# Revit family: VAD_Roof_Exhauster
name_source: partatom
category: Mechanical Equipment
units: mm (PartAtom-declared; Revit-internal decimal feet)

## family parameters
Always vertical = Yes
Cut with Voids When Loaded = No
Part Type = Normal
Room Calculation Point = No
Round Connector Dimension = Use Diameter
Shared = No
Work Plane-Based = No

## types (9) — shared parameters
0 = 0' - 0"
1" = 0' - 1"
1.5 = 0' - 1 1/2"
2" = 0' - 2"
2' = 2' - 0"
3" = 0' - 3"
30 = 30.00°
4" = 0' - 4"
60 = 60.00°
Manufacturer = Loren Cook Company
Model = VAD
ONE EIGTH = 0' - 0 1/8"
P = 0' - 0 9/16"
P/2 = 0' - 0 9/32"
Type Comments = Fixed Pitch Vane Axial Roof Exhauster Direct Drive Arrangement 4
URL = www.lorencook.com

## per-type parameters (varying)
- 18_VAD_ROOF_EXHAUSTER: (A+.25")/2=0' - 9 1/8"; (B/2)+2"=1' - 0 5/8"; (E-.25")/2=0' - 9 3/8"; (E/2)-2"=0' - 7 1/2"; (H-(A/2))/2=0' - 9 1/8"; (T_SQ+.25")/2=1' - 2 1/8"; -(E-.25")/2=-0' - 9 3/8"; -(E/2)+2"=-0' - 7 1/2"; -E/2=-0' - 9 1/2"; A=1' - 6"; A/2=0' - 9"; A/3=0' - 7 3/16"; B=1' - 9 1/4"; B/2=0' - 10 5/8"; C=1' - 7 3/4"; C/2=0' - 9 7/8"; C/2+L=1' - 10 5/16"; E=1' - 7"; E-2"=1' - 5"; E/2=0' - 9 1/2"; F=0' - 0 7/16"; F/2=0' - 0 7/32"; G=12' - 0"; H=2' - 3 1/4"; H+L=3' - 3 11/16"; H-(A/2)=1' - 6 1/4"; J=0' - 0 7/8"; J+J=0' - 1 3/4"; K=2' - 3 1/4"; K/2=1' - 1 5/8"; L=1' - 0 7/16"; L-(C/2)=0' - 2 9/16"; L-.125"=1' - 0 5/16"; M=1' - 9"; M/2=0' - 10 1/2"; N=0' - 8 1/2"; RO=1' - 11 1/2"; RO/2=0' - 11 3/4"; T_SQ=2' - 4"; UP_A=3' - 5"
- 21_VAD_ROOF_EXHAUSTER: (A+.25")/2=0' - 10 5/8"; (B/2)+2"=1' - 2 1/8"; (E-.25")/2=0' - 9 7/8"; (E/2)-2"=0' - 8"; (H-(A/2))/2=0' - 10 1/2"; (T_SQ+.25")/2=1' - 4 1/8"; -(E-.25")/2=-0' - 9 7/8"; -(E/2)+2"=-0' - 8"; -E/2=-0' - 10"; A=1' - 9"; A/2=0' - 10 1/2"; A/3=0' - 8 13/32"; B=2' - 0 1/4"; B/2=1' - 0 1/8"; C=1' - 10 3/4"; C/2=0' - 11 3/8"; C/2+L=2' - 1 5/16"; E=1' - 8"; E-2"=1' - 6"; E/2=0' - 10"; F=0' - 0 7/16"; F/2=0' - 0 7/32"; G=12' - 0"; H=2' - 7 1/2"; H+L=3' - 9 7/16"; H-(A/2)=1' - 9"; J=0' - 0 7/8"; J+J=0' - 1 3/4"; K=2' - 5 1/4"; K/2=1' - 2 5/8"; L=1' - 1 15/16"; L-(C/2)=0' - 2 9/16"; L-.125"=1' - 1 13/16"; M=2' - 0"; M/2=1' - 0"; N=0' - 10"; RO=2' - 3 1/2"; RO/2=1' - 1 3/4"; T_SQ=2' - 8"; UP_A=3' - 6"
- 26_VAD_ROOF_EXHAUSTER: (A+.25")/2=1' - 1 1/8"; (B/2)+2"=1' - 5 5/32"; (E-.25")/2=0' - 10 7/8"; (E/2)-2"=0' - 9"; (H-(A/2))/2=0' - 10 3/4"; (T_SQ+.25")/2=1' - 6 1/8"; -(E-.25")/2=-0' - 10 7/8"; -(E/2)+2"=-0' - 9"; -E/2=-0' - 11"; A=2' - 2"; A/2=1' - 1"; A/3=0' - 10 13/32"; B=2' - 6 5/16"; B/2=1' - 3 5/32"; C=2' - 4"; C/2=1' - 2"; C/2+L=2' - 6 11/16"; E=1' - 10"; E-2"=1' - 8"; E/2=0' - 11"; F=0' - 0 7/16"; F/2=0' - 0 7/32"; G=12' - 0"; H=2' - 10 1/2"; H+L=4' - 3 3/16"; H-(A/2)=1' - 9 1/2"; J=0' - 0 15/16"; J+J=0' - 1 7/8"; K=2' - 6 1/8"; K/2=1' - 3 1/16"; L=1' - 4 11/16"; L-(C/2)=0' - 2 11/16"; L-.125"=1' - 4 9/16"; M=2' - 5 9/16"; M/2=1' - 2 25/32"; N=1' - 0 13/16"; RO=2' - 7 1/2"; RO/2=1' - 3 3/4"; T_SQ=3' - 0"; UP_A=3' - 9"
- 29_VAD_ROOF_EXHAUSTER: (A+.25")/2=1' - 2 5/8"; (B/2)+2"=1' - 6 21/32"; (E-.25")/2=1' - 0 3/8"; (E/2)-2"=0' - 10 1/2"; (H-(A/2))/2=1' - 1"; (T_SQ+.25")/2=1' - 9 1/8"; -(E-.25")/2=-1' - 0 3/8"; -(E/2)+2"=-0' - 10 1/2"; -E/2=-1' - 0 1/2"; A=2' - 5"; A/2=1' - 2 1/2"; A/3=0' - 11 19/32"; B=2' - 9 5/16"; B/2=1' - 4 21/32"; C=2' - 7"; C/2=1' - 3 1/2"; C/2+L=2' - 9 3/4"; E=2' - 1"; E-2"=1' - 11"; E/2=1' - 0 1/2"; F=0' - 0 7/16"; F/2=0' - 0 7/32"; G=12' - 0"; H=3' - 4 1/2"; H+L=4' - 10 3/4"; H-(A/2)=2' - 2"; J=0' - 0 15/16"; J+J=0' - 1 7/8"; K=2' - 10 1/8"; K/2=1' - 5 1/16"; L=1' - 6 1/4"; L-(C/2)=0' - 2 3/4"; L-.125"=1' - 6 1/8"; M=2' - 8 5/8"; M/2=1' - 4 5/16"; N=1' - 2 5/16"; RO=3' - 1 1/2"; RO/2=1' - 6 3/4"; T_SQ=3' - 6"; UP_A=4' - 0"
- 36_VAD_ROOF_EXHAUSTER: (A+.25")/2=1' - 6 1/8"; (B/2)+2"=1' - 10 5/32"; (E-.25")/2=1' - 3 7/8"; (E/2)-2"=1' - 2"; (H-(A/2))/2=1' - 1 3/4"; (T_SQ+.25")/2=2' - 0 1/8"; -(E-.25")/2=-1' - 3 7/8"; -(E/2)+2"=-1' - 2"; -E/2=-1' - 4"; A=3' - 0"; A/2=1' - 6"; A/3=1' - 2 13/32"; B=3' - 4 5/16"; B/2=1' - 8 5/32"; C=3' - 2"; C/2=1' - 7"; C/2+L=3' - 5 1/4"; E=2' - 8"; E-2"=2' - 6"; E/2=1' - 4"; F=0' - 0 9/16"; F/2=0' - 0 9/32"; G=16' - 0"; H=3' - 9 1/2"; H+L=5' - 7 3/4"; H-(A/2)=2' - 3 1/2"; J=0' - 0 15/16"; J+J=0' - 1 7/8"; K=3' - 4 1/8"; K/2=1' - 8 1/16"; L=1' - 10 1/4"; L-(C/2)=0' - 3 1/4"; L-.125"=1' - 10 1/8"; M=3' - 4 5/8"; M/2=1' - 8 5/16"; N=1' - 6 5/16"; RO=3' - 7 1/2"; RO/2=1' - 9 3/4"; T_SQ=4' - 0"; UP_A=5' - 1"
- 42_VAD_ROOF_EXHAUSTER: (A+.25")/2=1' - 9 1/8"; (B/2)+2"=2' - 0 21/32"; (E-.25")/2=1' - 6 3/8"; (E/2)-2"=1' - 4 1/2"; (H-(A/2))/2=1' - 2 3/4"; (T_SQ+.25")/2=2' - 3 1/8"; -(E-.25")/2=-1' - 6 3/8"; -(E/2)+2"=-1' - 4 1/2"; -E/2=-1' - 6 1/2"; A=3' - 6"; A/2=1' - 9"; A/3=1' - 4 13/16"; B=3' - 9 5/16"; B/2=1' - 10 21/32"; C=3' - 8 3/8"; C/2=1' - 10 3/16"; C/2+L=3' - 11 3/8"; E=3' - 1"; E-2"=2' - 11"; E/2=1' - 6 1/2"; F=0' - 0 9/16"; F/2=0' - 0 9/32"; G=16' - 0"; H=4' - 2 1/2"; H+L=6' - 3 11/16"; H-(A/2)=2' - 5 1/2"; J=0' - 0 15/16"; J+J=0' - 1 7/8"; K=4' - 0 1/8"; K/2=2' - 0 1/16"; L=2' - 1 3/16"; L-(C/2)=0' - 3"; L-.125"=2' - 1 1/16"; M=4' - 0 3/4"; M/2=2' - 0 3/8"; N=1' - 9 3/8"; RO=4' - 1 1/2"; RO/2=2' - 0 3/4"; T_SQ=4' - 6"; UP_A=5' - 6"
- 48_VAD_ROOF_EXHAUSTER: (A+.25")/2=2' - 0 1/8"; (B/2)+2"=2' - 4 19/32"; (E-.25")/2=1' - 8 7/8"; (E/2)-2"=1' - 7"; (H-(A/2))/2=1' - 3"; (T_SQ+.25")/2=2' - 5 1/4"; -(E-.25")/2=-1' - 8 7/8"; -(E/2)+2"=-1' - 7"; -E/2=-1' - 9"; A=4' - 0"; A/2=2' - 0"; A/3=1' - 7 3/16"; B=4' - 5 3/16"; B/2=2' - 2 19/32"; C=4' - 2 1/2"; C/2=2' - 1 1/4"; C/2+L=4' - 5 1/2"; E=3' - 6"; E-2"=3' - 4"; E/2=1' - 9"; F=0' - 0 9/16"; F/2=0' - 0 9/32"; G=16' - 0"; H=4' - 6"; H+L=6' - 10 1/4"; H-(A/2)=2' - 6"; J=0' - 0 15/16"; J+J=0' - 1 7/8"; K=4' - 6 1/8"; K/2=2' - 3 1/16"; L=2' - 4 1/4"; L-(C/2)=0' - 3"; L-.125"=2' - 4 1/8"; M=4' - 4 3/4"; M/2=2' - 2 3/8"; N=2' - 0 3/8"; RO=4' - 5 3/4"; RO/2=2' - 2 7/8"; T_SQ=4' - 10 1/4"; UP_A=6' - 11 1/2"
- 54_VAD_ROOF_EXHAUSTER: (A+.25")/2=2' - 3 1/8"; (B/2)+2"=2' - 7 23/32"; (E-.25")/2=1' - 10 7/8"; (E/2)-2"=1' - 9"; (H-(A/2))/2=1' - 4 1/4"; (T_SQ+.25")/2=2' - 8 1/4"; -(E-.25")/2=-1' - 10 7/8"; -(E/2)+2"=-1' - 9"; -E/2=-1' - 11"; A=4' - 6"; A/2=2' - 3"; A/3=1' - 9 19/32"; B=4' - 11 7/16"; B/2=2' - 5 23/32"; C=4' - 8 1/2"; C/2=2' - 4 1/4"; C/2+L=4' - 11 1/2"; E=3' - 10"; E-2"=3' - 8"; E/2=1' - 11"; F=0' - 0 9/16"; F/2=0' - 0 9/32"; G=16' - 0"; H=4' - 11 1/2"; H+L=7' - 6 3/4"; H-(A/2)=2' - 8 1/2"; J=0' - 1"; J+J=0' - 2"; K=5' - 0"; K/2=2' - 6"; L=2' - 7 1/4"; L-(C/2)=0' - 3"; L-.125"=2' - 7 1/8"; M=4' - 11"; M/2=2' - 5 1/2"; N=2' - 3 1/2"; RO=4' - 11 3/4"; RO/2=2' - 5 7/8"; T_SQ=5' - 4 1/4"; UP_A=7' - 3 1/2"
- 60_VAD_ROOF_EXHAUSTER: (A+.25")/2=2' - 6 1/8"; (B/2)+2"=2' - 10 23/32"; (E-.25")/2=1' - 10 7/8"; (E/2)-2"=1' - 9"; (H-(A/2))/2=1' - 5 1/2"; (T_SQ+.25")/2=2' - 11 1/4"; -(E-.25")/2=-1' - 10 7/8"; -(E/2)+2"=-1' - 9"; -E/2=-1' - 11"; A=5' - 0"; A/2=2' - 6"; A/3=2' - 0"; B=5' - 5 7/16"; B/2=2' - 8 23/32"; C=5' - 3 1/4"; C/2=2' - 7 5/8"; C/2+L=5' - 6 7/8"; E=3' - 10"; E-2"=3' - 8"; E/2=1' - 11"; F=0' - 0 9/16"; F/2=0' - 0 9/32"; G=16' - 0"; H=5' - 5"; H+L=8' - 4 1/4"; H-(A/2)=2' - 11"; J=0' - 1"; J+J=0' - 2"; K=5' - 7"; K/2=2' - 9 1/2"; L=2' - 11 1/4"; L-(C/2)=0' - 3 5/8"; L-.125"=2' - 11 1/8"; M=5' - 6"; M/2=2' - 9"; N=2' - 7"; RO=5' - 5 3/4"; RO/2=2' - 8 7/8"; T_SQ=5' - 10 1/4"; UP_A=7' - 3 1/2"

## geometry (parser evidence)
native form markers: Sweep x1
no freeform markers — native parametric forms only
